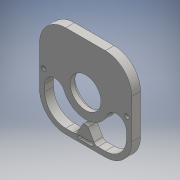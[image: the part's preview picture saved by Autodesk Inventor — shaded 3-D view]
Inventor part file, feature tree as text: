
AUTODESK INVENTOR PART (.ipt)
format: ipt  version: 2016 (Build 200138000, 138)  size: 199,680 bytes
history: native  units: mm
features: extrude x6, sketch x6, fillet x2, chamfer x1, projected_geometry x1
ambient origin geometry x8: Origin, YZ Plane, XZ Plane, XY Plane, X Axis, Y Axis, Z Axis, Center Point
bodies: Solid1 (feature_tree)
feature tree (16):
  extrude  "Extrusion1"  Depth=105.0mm
  fillet  "Fillet1"  Radius=10.0mm
  extrude  "Extrusion2"  Depth=10.0mm
  chamfer  "Chamfer1"  Distance=10.0mm
  extrude  "Extrusion3"  Depth=6.0mm
  extrude  "Extrusion4"  Depth=4.0mm
  extrude  "Extrusion5"  Depth=10.0mm TaperAngle=0.0deg
  fillet  "Fillet2"  Radius=5.0mm
  extrude  "Extrusion6"  Depth=5.0mm
  sketch  "Sketch1"  dims[d0=105.0mm d1=105.0mm d2=10.0mm d3=0.0mm]
  sketch  "Sketch2"  dims[d4=30.0mm d5=35.0mm d6=10.0mm d7=0.0mm]
  sketch  "Sketch3"  dims[d8=5.0mm d9=2.0mm d10=45.0deg d11=6.0mm]
  projected_geometry  "Projected Loop1"
  sketch  "Sketch5"  dims[d12=4.0mm d13=23.0mm]
  sketch  "Sketch6"  dims[d14=23.0mm d15=10.0mm d16=0.0mm d21=5.0mm]
  sketch  "Sketch7"  dims[d22=5.0mm d23=5.0mm d24=5.0mm d25=10.0mm d26=0.0mm d27=38.0mm d28=38.0mm d29=21.0mm d30=5.5mm d31=11.0mm d32=10.0mm d33=0.0mm d34=5.0mm d37=14.0mm d38=4.0mm d39=4.0mm d40=10.0mm d41=0.0mm]
